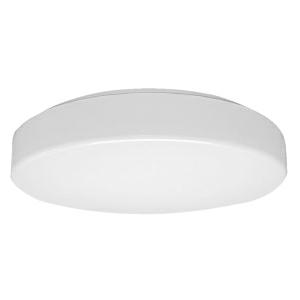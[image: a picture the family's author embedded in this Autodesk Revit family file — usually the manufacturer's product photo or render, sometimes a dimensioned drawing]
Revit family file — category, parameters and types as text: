
# Revit family: oblo_fit_-_oba_2000_840_d_00813351_19c0
name_source: partatom
category: Lighting Fixtures
units: mm (PartAtom-declared; Revit-internal decimal feet)

## family parameters
Cut with Voids When Loaded = No
Host = Face
Light Source = No
Part Type = Normal
Room Calculation Point = No
Round Connector Dimension = Use Diameter
Shared = No

## types (1)
- OBLO.fit - OBA 2000/840/D (1 x LED, 2100 lm, 4000K)
    Apparent Load = 22 VA
    Approval mark = CE
    CIE Flux Codes = 41 72 91 84 100
    Color Rendering = 80-89
    Color Temperature = 4000K
    Control Gear = Electronic ballast
    Default Elevation = 1800 mm
    Description = OBA 2000/840/D|Surface-mounted luminaire.|light source:   Cold white   |work equipment: Power supply unit|luminous flux: 2100 lm|light distribution: Direct|class of protection: I|technology: Continuously dimmable|mains lead: Direct power supply|glare control: without|special features: DALI Load 1x|
    Frequency = 50 Hz, 60 Hz
    Height = 85 mm
    Lamp = 1 x LED
    Lamp Light Flux = 2100 lm
    Lamp count = 1
    Length = 370 mm
    Luminous efficacy = 95 lm/W
    Manufacturer = Waldmann
    ModVariant = No
    Model = 00813351
    Mounting Place = Ceiling
    Mounting Type = Surface mounted
    Number of Poles = 1
    OnlyDefault = Yes
    Power Factor = 1
    Product Name = OBLO.fit - OBA 2000/840/D
    Product group = Ceiling mounted luminaire
    ProductGroupID = 3
    Protection Class = Protection class I
    Protection Degree = IP 40
    RLX_Detail_Level = 1
    RLX_Emergency_Light_Flux = 0 lm
    RLX_Emergency_Type = 0
    RLX_Emergency_Type_DB = No
    RlxData = <blob elided: 22373 chars, md5=02775776>
    Socket = socket
    Standby Power = 0 W
    System Light Flux = 2100 lm
    System Power = 22 W
    Type Comments = Product without accessories
    Type Image = oblo_led.jpg
    URL = http://relux.com
    VarID = ---
    Voltage = 230 V
    Voltage Range = 220-240 V
    Weight = 0.00 kg
    Width = 0 mm  [stored 0 ft]

note: [stored X ft] marks values corroborated as IEEE doubles in the binary element streams (Revit-internal decimal feet)

## geometry (parser evidence)
native form markers: Blend x4, Sweep x15
no freeform markers — native parametric forms only
